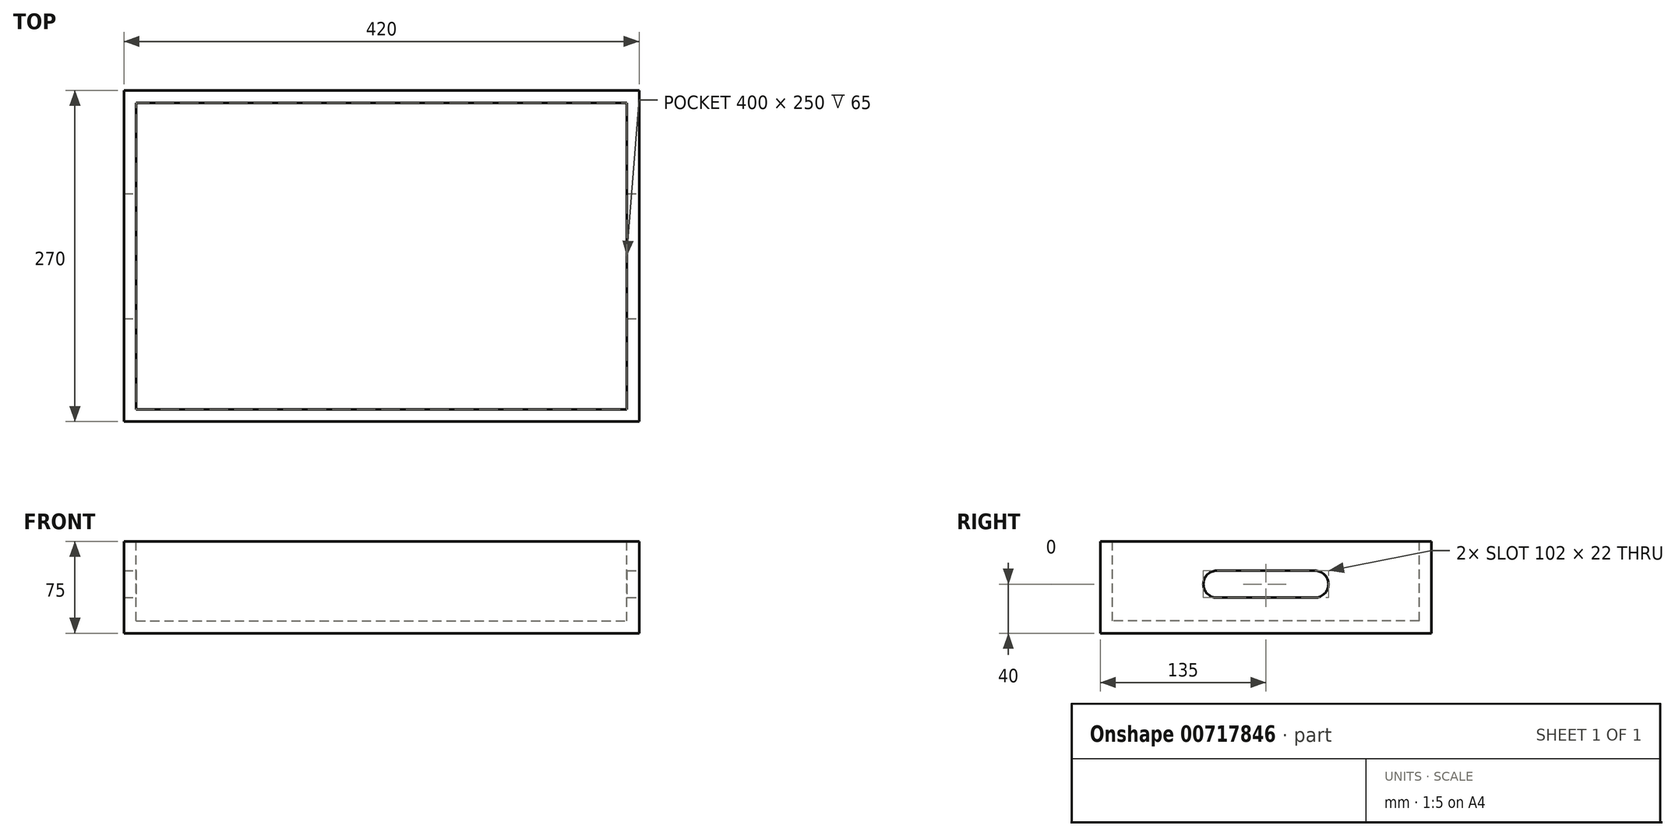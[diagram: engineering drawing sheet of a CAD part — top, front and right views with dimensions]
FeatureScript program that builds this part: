
annotation { "Feature Type Name" : "Feature", "Feature Type Description" : "" }
export const myFeature = defineFeature(function(context is Context, id is Id, definition is map)
    precondition{}
    {
        {
            var Q0;
            Q0=qCreatedBy(makeId("Front.planeOp"),FACE);
            var sketch = newSketch(context, id + "F0", { "sketchPlane" : qUnion([Q0])});
            skLineSegment(sketch, "E0.bottom", {"start": v(0, 0) * mm, "end": v(420, 0) * mm});
            skLineSegment(sketch, "E0.top", {"start": v(0, 75) * mm, "end": v(420, 75) * mm});
            skLineSegment(sketch, "E0.left", {"start": v(0, 0) * mm, "end": v(0, 75) * mm});
            skLineSegment(sketch, "E0.right", {"start": v(420, 0) * mm, "end": v(420, 75) * mm});
            skSolve(sketch);
        }
        {
            var Q0;
            Q0=makeQuery(id+"F0.imprint","IMPRINT",FACE,{"disambiguationData":[TD([[makeQuery(id+"F0.imprint","IMPRINT",EDGE,{"derivedFrom":sQuery(id+"F0.wireOp",EDGE,"E0.bottom")}),1.0]])]});
            extrude(context, id + "F1", {"entities" : qUnion([Q0]), "oppositeDirection" : true, "depth" : 270 * mm, "offsetDistance" : 25 * mm});
        }
        {
            var Q0;
            Q0=makeQuery(id+"F1.opExtrude","SWEPT_FACE",FACE,{"disambiguationData":[OSD([sQuery(id+"F0.wireOp",EDGE,"E0.top")])]});
            var sketch = newSketch(context, id + "F2", { "sketchPlane" : qUnion([Q0])});
            skLineSegment(sketch, "E1.0", {"start": v(10, 260) * mm, "end": v(410, 260) * mm});
            skLineSegment(sketch, "E2.0", {"start": v(10, 260) * mm, "end": v(10, 10) * mm});
            skLineSegment(sketch, "E3.0", {"start": v(10, 10) * mm, "end": v(410, 10) * mm});
            skLineSegment(sketch, "E4.0", {"start": v(410, 260) * mm, "end": v(410, 10) * mm});
            skSolve(sketch);
        }
        {
            var Q0;
            Q0=qSketchRegion(id+"F2",true);
            extrude(context, id + "F3", {"entities" : qUnion([Q0]), "operationType" : NewBodyOperationType.REMOVE, "oppositeDirection" : true, "depth" : 65 * mm, "offsetDistance" : 25 * mm});
        }
        {
            var Q0;
            Q0=makeQuery(id+"F1.opExtrude","SWEPT_FACE",FACE,{"disambiguationData":[OSD([sQuery(id+"F0.wireOp",EDGE,"E0.right")])]});
            var sketch = newSketch(context, id + "F4", { "sketchPlane" : qUnion([Q0])});
            skArc(sketch, "E5", {"start": v(95, 51) * mm, "mid": v(84, 40) * mm, "end": v(95, 29) * mm});
            skArc(sketch, "E6", {"start": v(175, 29) * mm, "mid": v(186, 40) * mm, "end": v(175, 51) * mm});
            skPoint(sketch, "E7", {"position": v(135, 75) * mm});
            skLineSegment(sketch, "E8", {"start": v(95, 51) * mm, "end": v(175, 51) * mm});
            skLineSegment(sketch, "E9", {"start": v(175, 29) * mm, "end": v(95, 29) * mm});
            skPoint(sketch, "E10", {"position": v(0, 75) * mm});
            skPoint(sketch, "E11", {"position": v(270, 75) * mm});
            skSolve(sketch);
        }
        {
            var Q0;
            Q0=makeQuery(id+"F4.imprint","IMPRINT",FACE,{"disambiguationData":[TD([[makeQuery(id+"F4.imprint","IMPRINT",EDGE,{"derivedFrom":sQuery(id+"F4.wireOp",EDGE,"E5")}),1.0]])]});
            extrude(context, id + "F5", {"entities" : qUnion([Q0]), "operationType" : NewBodyOperationType.REMOVE, "endBound" : BoundingType.THROUGH_ALL, "oppositeDirection" : true, "depth" : 25 * mm, "offsetDistance" : 25 * mm});
        }
    });
